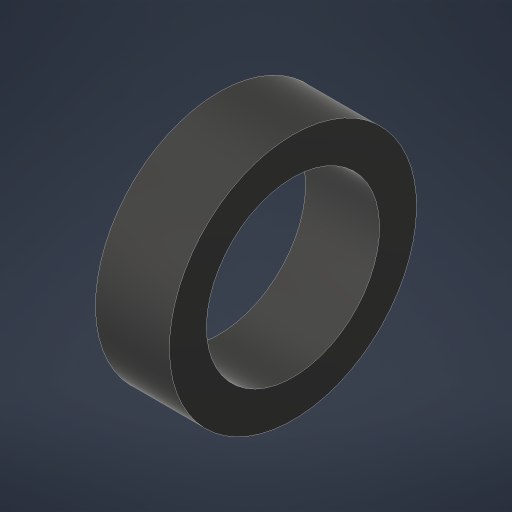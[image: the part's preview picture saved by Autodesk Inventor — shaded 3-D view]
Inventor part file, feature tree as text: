
AUTODESK INVENTOR PART (.ipt)
format: ipt  version: 2023.4 (Build 274418000, 418)  size: 169,984 bytes
history: native  units: in
note: dims shown in document units (in); Inventor stores cm internally (conversion verified against a paired STEP export)
features: extrude x1, sketch x1
ambient origin geometry x8: Origin, YZ Plane, XZ Plane, XY Plane, X Axis, Y Axis, Z Axis, Center Point
bodies: Solid1 (feature_tree)
feature tree (2):
  extrude  "Extrusion1"  Depth=0.125in
  sketch  "Sketch1"  dims[d0=0.585in d1=0.125in d2=0.25in d3=0.0in]
